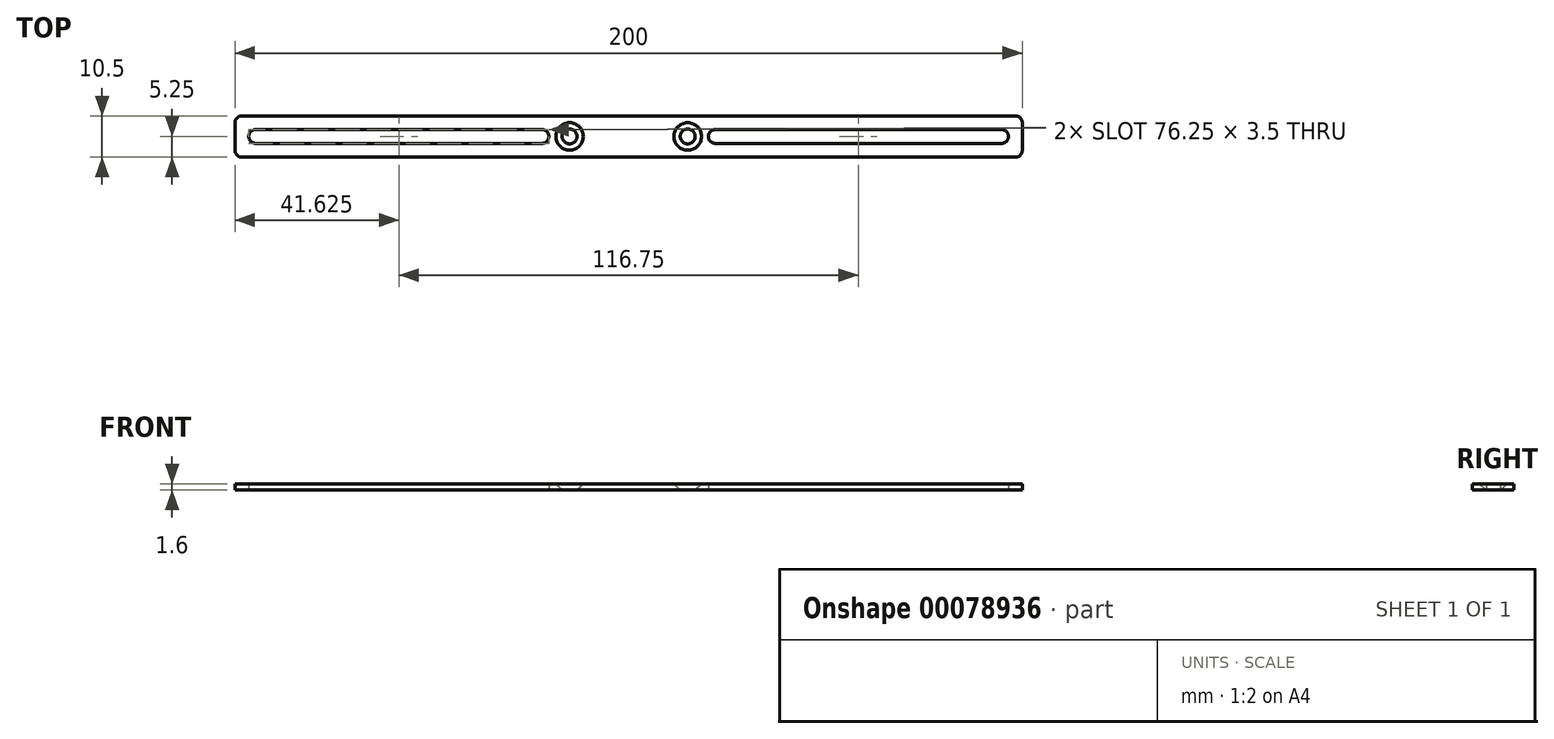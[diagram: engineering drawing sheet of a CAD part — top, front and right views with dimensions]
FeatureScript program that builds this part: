
annotation { "Feature Type Name" : "Feature", "Feature Type Description" : "" }
export const myFeature = defineFeature(function(context is Context, id is Id, definition is map)
    precondition{}
    {
        {
            assignVariable(context, id + "F0", {"name" : "ScrewDiameter", "anyValue" : 3.5});
        }
        {
            var Q0;
            Q0=qCreatedBy(makeId("Top.planeOp"),FACE);
            var sketch = newSketch(context, id + "F1", { "sketchPlane" : qUnion([Q0])});
            skLineSegment(sketch, "E0", {"start": v(0, 0) * mm, "end": v(200, 0) * mm});
            skLineSegment(sketch, "E1", {"start": v(200, 0) * mm, "end": v(200, 10.5) * mm});
            skLineSegment(sketch, "E2", {"start": v(200, 10.5) * mm, "end": v(0, 10.5) * mm});
            skLineSegment(sketch, "E3", {"start": v(0, 10.5) * mm, "end": v(0, 0) * mm});
            skLineSegment(sketch, "E4", {"start": v(100, 10.5) * mm, "end": v(100, 0) * mm, "construction": true});
            skCircle(sketch, "E5", {"center": v(85, 5.25) * mm, "radius": 1.75 * mm});
            skPoint(sketch, "E5.centerSnap0", {"position": v(100, 5.25) * mm});
            skArc(sketch, "E6", {"start": v(78, 3.5) * mm, "mid": v(79.75, 5.25) * mm, "end": v(78, 7) * mm});
            skLineSegment(sketch, "E7", {"start": v(78, 7) * mm, "end": v(5.25, 7) * mm});
            skLineSegment(sketch, "E8", {"start": v(78, 3.5) * mm, "end": v(5.25, 3.5) * mm});
            skArc(sketch, "E9", {"start": v(5.25, 7) * mm, "mid": v(3.5, 5.25) * mm, "end": v(5.25, 3.5) * mm});
            skArc(sketch, "E10.MirrorCS", {"start": v(194.75, 7) * mm, "mid": v(196.5, 5.25) * mm, "end": v(194.75, 3.5) * mm});
            skLineSegment(sketch, "E11.MirrorCS", {"start": v(122, 7) * mm, "end": v(194.75, 7) * mm});
            skLineSegment(sketch, "E12.MirrorCS", {"start": v(122, 3.5) * mm, "end": v(194.75, 3.5) * mm});
            skArc(sketch, "E13.MirrorCS", {"start": v(122, 3.5) * mm, "mid": v(120.25, 5.25) * mm, "end": v(122, 7) * mm});
            skCircle(sketch, "E14.MirrorC", {"center": v(115, 5.25) * mm, "radius": 1.75 * mm});
            skLineSegment(sketch, "E15", {"start": v(83.25, 10.5) * mm, "end": v(83.25, 0) * mm, "construction": true});
            skSolve(sketch);
        }
        {
            var Q0;
            Q0=makeQuery(id+"F1.imprint","IMPRINT",FACE,{"disambiguationData":[TD([[makeQuery(id+"F1.imprint","IMPRINT",EDGE,{"derivedFrom":sQuery(id+"F1.wireOp",EDGE,"E0")}),1.0]])]});
            extrude(context, id + "F2", {"entities" : qUnion([Q0]), "depth" : 1.6 * mm});
        }
        {
            var Q0;
            Q0=makeQuery(id+"F2.opExtrude","SWEPT_EDGE",EDGE,{"disambiguationData":[OSD([sQuery(id+"F1.wireOp",EDGE,"E2"),sQuery(id+"F1.wireOp",EDGE,"E3")])]});
            var Q1;
            Q1=makeQuery(id+"F2.opExtrude","SWEPT_EDGE",EDGE,{"disambiguationData":[OSD([sQuery(id+"F1.wireOp",EDGE,"E0"),sQuery(id+"F1.wireOp",EDGE,"E3")])]});
            var Q2;
            Q2=makeQuery(id+"F2.opExtrude","SWEPT_EDGE",EDGE,{"disambiguationData":[OSD([sQuery(id+"F1.wireOp",EDGE,"E0"),sQuery(id+"F1.wireOp",EDGE,"E1")])]});
            var Q3;
            Q3=makeQuery(id+"F2.opExtrude","SWEPT_EDGE",EDGE,{"disambiguationData":[OSD([sQuery(id+"F1.wireOp",EDGE,"E1"),sQuery(id+"F1.wireOp",EDGE,"E2")])]});
            var Q4;
            Q4=makeQuery(id+"F2.opExtrude","SWEPT_EDGE",EDGE,{"disambiguationData":[OSD([sQuery(id+"F1.wireOp",EDGE,"E0"),sQuery(id+"F1.wireOp",EDGE,"SPCWLJXN-8ILj-DUJN-xmoq-a1Nes1dhze3g")])]});
            var Q5;
            Q5=makeQuery(id+"F2.opExtrude","SWEPT_EDGE",EDGE,{"disambiguationData":[OSD([sQuery(id+"F1.wireOp",EDGE,"SPCWLJXN-8ILj-DUJN-xmoq-a1Nes1dhze3g"),sQuery(id+"F1.wireOp",EDGE,"M6f6fjkd-6Qvh-Byrq-l6gj-bQObs1zztFZM")])]});
            var Q6;
            Q6=makeQuery(id+"F2.opExtrude","SWEPT_EDGE",EDGE,{"disambiguationData":[OSD([sQuery(id+"F1.wireOp",EDGE,"12b26aed-90c2-433f-909a-6cbc3283f18a2.MirrorCS"),sQuery(id+"F1.wireOp",EDGE,"12b26aed-90c2-433f-909a-6cbc3283f18a3.MirrorCS")])]});
            var Q7;
            Q7=makeQuery(id+"F2.opExtrude","SWEPT_EDGE",EDGE,{"disambiguationData":[OSD([sQuery(id+"F1.wireOp",EDGE,"E0"),sQuery(id+"F1.wireOp",EDGE,"12b26aed-90c2-433f-909a-6cbc3283f18a3.MirrorCS")])]});
            fillet(context, id + "F3", {"entities" : qUnion([Q0, Q1, Q2, Q3, Q4, Q5, Q6, Q7]), "radius" : (getVariable(context, 'ScrewDiameter') / 2) * mm, "tangentPropagation" : true, "allowEdgeOverflow" : false});
        }
        {
            var Q0;
            Q0=makeQuery(id+"F2.opExtrude","CAP_EDGE",EDGE,{"disambiguationData":[OSD([sQuery(id+"F1.wireOp",EDGE,"E5")])],"isStart":false});
            var Q1;
            Q1=makeQuery(id+"F2.opExtrude","CAP_EDGE",EDGE,{"disambiguationData":[OSD([sQuery(id+"F1.wireOp",EDGE,"E14.MirrorC")])],"isStart":false});
            chamfer(context, id + "F4", {"entities" : qUnion([Q0, Q1]), "width" : (getVariable(context, 'ScrewDiameter') / 2) * mm, "tangentPropagation" : true});
        }
    });
